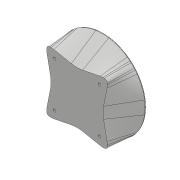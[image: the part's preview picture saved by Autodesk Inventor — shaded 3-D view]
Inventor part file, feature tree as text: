
AUTODESK INVENTOR PART (.ipt)
format: ipt  version: 2018 (Build 220112000, 112)  size: 2,090,496 bytes
history: native  units: mm
features: sketch x39, projected_geometry x35, extrude x32, fillet x9, hole x5, chamfer x5, other x2, mirror x1, revolve x1, shell x1, pattern_circular x1, plane x1, loft x1
ambient origin geometry x8: Origin, YZ Plane, XZ Plane, XY Plane, X Axis, Y Axis, Z Axis, Center Point
bodies: Solid1 (feature_tree)
feature tree (133):
  extrude  "Extrusion1"  Depth=45.0mm
  extrude  "Extrusion2"  Depth=2.25mm
  hole  "Hole1"  [1 undecoded]
  hole  "Hole2"  [1 undecoded]
  fillet  "Fillet1"  Radius=14.0mm
  extrude  "Extrusion3"  Depth=18.5mm
  extrude  "Extrusion4"  Depth=20.5mm
  extrude  "Extrusion5"  Depth=2.195mm
  extrude  "Extrusion6"  Depth=20.5mm
  hole  "Hole3"  [1 undecoded]
  extrude  "Extrusion7"  Depth=0.5mm
  extrude  "Extrusion8"  Depth=5.0mm TaperAngle=0.0deg
  extrude  "Extrusion9"  Depth=24.5mm
  extrude  "Extrusion10"  Depth=10.0mm
  extrude  "Extrusion11"  Depth=14.5mm
  extrude  "Extrusion12"  Depth=14.5mm
  extrude  "Extrusion13"  Depth=5.0mm
  extrude  "Extrusion14"  Depth=2.25mm
  extrude  "Extrusion15"  Depth=5.0mm
  extrude  "Extrusion16"  Depth=9.0mm
  extrude  "Extrusion17"  Depth=4.0mm
  chamfer  "Chamfer1"  Distance=1.0mm
  fillet  "Fillet7"  Radius=20.7mm
  fillet  "Fillet8"  Radius=32.0mm
  mirror  "Mirror1"
  extrude  "Extrusion18"  Depth=1.0mm TaperAngle=0.0deg
  extrude  "Extrusion19"  Depth=8.0mm
  extrude  "Extrusion20"  Depth=0.2mm TaperAngle=0.0deg
  extrude  "Extrusion21"  Depth=0.5mm TaperAngle=0.0deg
  extrude  "Extrusion22"  Depth=3.0mm TaperAngle=0.0deg
  extrude  "Extrusion23"  Depth=0.2mm TaperAngle=0.0deg
  extrude  "Extrusion24"  Depth=2.5mm TaperAngle=45.0deg
  sketch  "Sketch35"  dims[d91=8.0mm d92=0.0mm d93=3.0mm d94=0.0mm]
  other  "Work Axis1"
  revolve  "Revolution1"  [1 undecoded]
  extrude  "Extrusion25"  Depth=4.0mm TaperAngle=0.0deg
  extrude  "Extrusion26"  Depth=19.2mm TaperAngle=0.0deg
  shell  "Shell1"  Thickness=52.1mm
  extrude  "Extrusion27"  Depth=9.0mm
  extrude  "Extrusion28"  Depth=25.0mm
  chamfer  "Chamfer4"  Distance=6.9mm
  chamfer  "Chamfer5"  Distance=2.5mm
  extrude  "Extrusion29"  Depth=5.0mm
  pattern_circular  "Circular Pattern1"  Angle=90.0deg  [1 undecoded]
  fillet  "Fillet11"  Radius=5.0mm
  fillet  "Fillet12"  Radius=105.0mm
  fillet  "Fillet13"  Radius=105.0mm
  fillet  "Fillet14"  Radius=5.0mm
  chamfer  "Chamfer6"  Distance=12.8mm
  hole  "Hole6"  [1 undecoded]
  extrude  "Extrusion30"  Depth=12.8mm
  fillet  "Fillet15"  Radius=12.8mm
  extrude  "Extrusion31"  Depth=20.0mm
  plane  "Work Plane1"
  loft  "Loft1"
  hole  "Hole8"  [1 undecoded]
  extrude  "Extrusion35"  Depth=6.0mm
  chamfer  "Chamfer7"  Distance=40.0mm
  fillet  "Fillet20"  Radius=8.0mm
  sketch  "Sketch1"  dims[d0=24.5mm d1=45.0mm]
  sketch  "Sketch2"  dims[d2=1.95mm d3=0.0mm d4=2.25mm]
  projected_geometry  "Projected Loop1"
  sketch  "Sketch3"  dims[d5=20.0mm d6=2.25mm]
  projected_geometry  "Projected Loop2"
  sketch  "Sketch4"  dims[d7=5.25mm d8=5.25mm d9=14.0mm]
  projected_geometry  "Projected Loop3"
  sketch  "Sketch5"  dims[d10=5.25mm d11=18.5mm]
  projected_geometry  "Projected Loop4"
  sketch  "Sketch6"  dims[d12=10.0mm d13=0.0mm d14=20.5mm]
  projected_geometry  "Projected Loop5"
  sketch  "Sketch7"  dims[d15=2.0mm d16=2.195mm]
  projected_geometry  "Projected Loop6"
  sketch  "Sketch8"  dims[d17=2.0mm]
  projected_geometry  "Projected Loop7"
  sketch  "Sketch9"  dims[d18=2.4mm d19=6.0mm d20=4.4mm d21=2.0mm d22=90.0deg d23=8.0mm d24=20.594885mm d25=20.5mm]
  projected_geometry  "Projected Loop8"
  projected_geometry  "Projected Loop9"
  sketch  "Sketch10"  dims[d26=26.65mm d27=2.0mm]
  projected_geometry  "Projected Loop10"
  projected_geometry  "Projected Loop11"
  sketch  "Sketch11"  dims[d28=2.0mm]
  projected_geometry  "Projected Loop12"
  sketch  "Sketch12"  dims[d29=2.4mm d30=6.0mm d31=4.4mm d32=2.0mm d33=90.0deg d34=8.0mm d35=20.594885mm d36=0.5mm]
  sketch  "Sketch13"  dims[d37=18.0mm d38=5.0mm d39=0.0mm]
  sketch  "Sketch14"  dims[d41=10.0mm d42=0.0mm d43=24.5mm]
  projected_geometry  "Projected Loop13"
  sketch  "Sketch15"  dims[d44=1.15mm d45=0.0mm d46=10.0mm]
  sketch  "Sketch16"  dims[d47=21.0mm d48=14.5mm]
  projected_geometry  "Projected Loop14"
  sketch  "Sketch17"  dims[d49=20.0mm d50=14.5mm]
  projected_geometry  "Projected Loop15"
  sketch  "Sketch18"  dims[d51=24.5mm d52=5.0mm]
  projected_geometry  "Projected Loop16"
  sketch  "Sketch19"  dims[d53=5.0mm d54=2.25mm]
  projected_geometry  "Projected Loop17"
  sketch  "Sketch20"  dims[d55=2.25mm d56=5.0mm]
  projected_geometry  "Projected Loop18"
  sketch  "Sketch22"  dims[d57=5.0mm d58=9.0mm]
  sketch  "Sketch25"  dims[d59=14.75mm d60=4.0mm d61=1.0mm d62=0.0mm d63=20.7mm]
  sketch  "Sketch27"  dims[d64=2.4mm d65=6.0mm d66=4.4mm d67=2.0mm d68=90.0deg d69=8.0mm d70=20.594885mm d72=32.0mm]
  projected_geometry  "Projected Loop22"
  sketch  "Sketch28"  dims[d73=5.0mm d74=0.0mm d75=1.0mm d76=0.0mm]
  projected_geometry  "Projected Loop23"
  sketch  "Sketch29"  dims[d77=12.25mm d78=0.0mm d80=8.0mm]
  projected_geometry  "Projected Loop24"
  sketch  "Sketch30"  dims[d81=4.5mm d82=0.0mm d84=0.2mm d85=0.0mm]
  projected_geometry  "Projected Loop25"
  sketch  "Sketch33"  dims[d86=21.0mm d87=0.5mm d88=0.0mm]
  projected_geometry  "Projected Loop26"
  sketch  "Sketch36"  dims[d95=5.0mm d96=0.0mm d98=0.2mm d99=0.0mm]
  projected_geometry  "Projected Loop27"
  sketch  "Sketch37"  dims[d100=0.2mm d101=0.0mm d102=2.5mm d103=2.0mm d104=45.0deg]
  projected_geometry  "Projected Loop28"
  sketch  "Sketch38"  dims[d105=1.5mm d114=0.5mm]
  projected_geometry  "Projected Loop29"
  projected_geometry  "Projected Loop30"
  projected_geometry  "Projected Loop31"
  projected_geometry  "Projected Loop32"
  sketch  "Sketch39"  dims[d115=22.55mm d116=0.0mm d128=4.0mm d129=0.0mm]
  projected_geometry  "Projected Loop33"
  projected_geometry  "Projected Loop34"
  sketch  "Sketch40"  dims[d130=4.0mm d131=0.0mm d132=19.2mm d133=0.0mm d134=52.1mm]
  projected_geometry  "Projected Loop35"
  sketch  "Sketch41"  dims[d135=6.8mm d136=0.0mm d137=9.0mm]
  projected_geometry  "Projected Loop36"
  sketch  "Sketch42"  dims[d138=9.0mm d139=25.0mm d140=6.9mm d141=0.0mm]
  sketch  "Sketch43"  dims[d142=5.2mm]
  projected_geometry  "Projected Loop37"
  sketch  "Sketch49"  dims[d143=5.2mm]
  other  "Edges1"
  sketch  "Sketch50"  dims[d144=5.2mm]
  sketch  "Sketch51"  dims[d145=5.2mm d146=2.5mm d147=0.0mm d148=5.0mm d149=90.0deg d150=5.0mm d151=105.0mm d152=105.0mm d153=5.0mm d154=0.0mm d156=12.8mm d157=12.8mm d158=12.8mm d159=12.8mm d160=20.0mm d161=20.0mm d162=20.0mm d163=6.0mm d164=40.0mm d165=0.0mm d166=8.0mm d167=40.0mm d168=0.0mm d169=40.0mm d170=0.0mm d178=5.1mm d179=2.45mm d180=45.0deg d181=4.1mm d182=2.45mm d183=45.0deg d184=10.0mm d185=10.0mm d186=40.0mm d187=0.0mm d188=40.0mm d189=360.0deg d191=5.1mm d192=25.0mm d193=50.0mm d194=50.0mm d195=5.0mm d196=2.0mm d197=45.0deg d198=110.0mm d199=77.781746mm d200=77.781746mm d201=6.4mm d202=6.0mm d203=12.6mm d204=2.0mm d205=90.0deg d206=8.0mm d207=20.594885mm d208=11.0mm d209=11.0mm d210=11.0mm d211=11.0mm d212=45.0mm d213=0.0mm d214=1.0mm d215=2.0mm d216=0.0mm d236=45.0mm d237=150.0mm d238=0.0mm d239=90.0deg d240=0.0mm d241=90.0deg d242=4.917mm d243=60.0mm d244=4.0mm d245=2.0mm d246=90.0deg d247=17.1mm d248=20.594885mm d249=45.0mm d250=0.0mm d251=1.0mm d252=2.0mm d253=45.0deg d254=1.0mm]
  projected_geometry  "Project Cut Edges1"
note: 7 required parameter values undecoded (feature->parameter linkage not recoverable at this tier; creation-order binding heuristic only, values carry confidence <= 0.55)